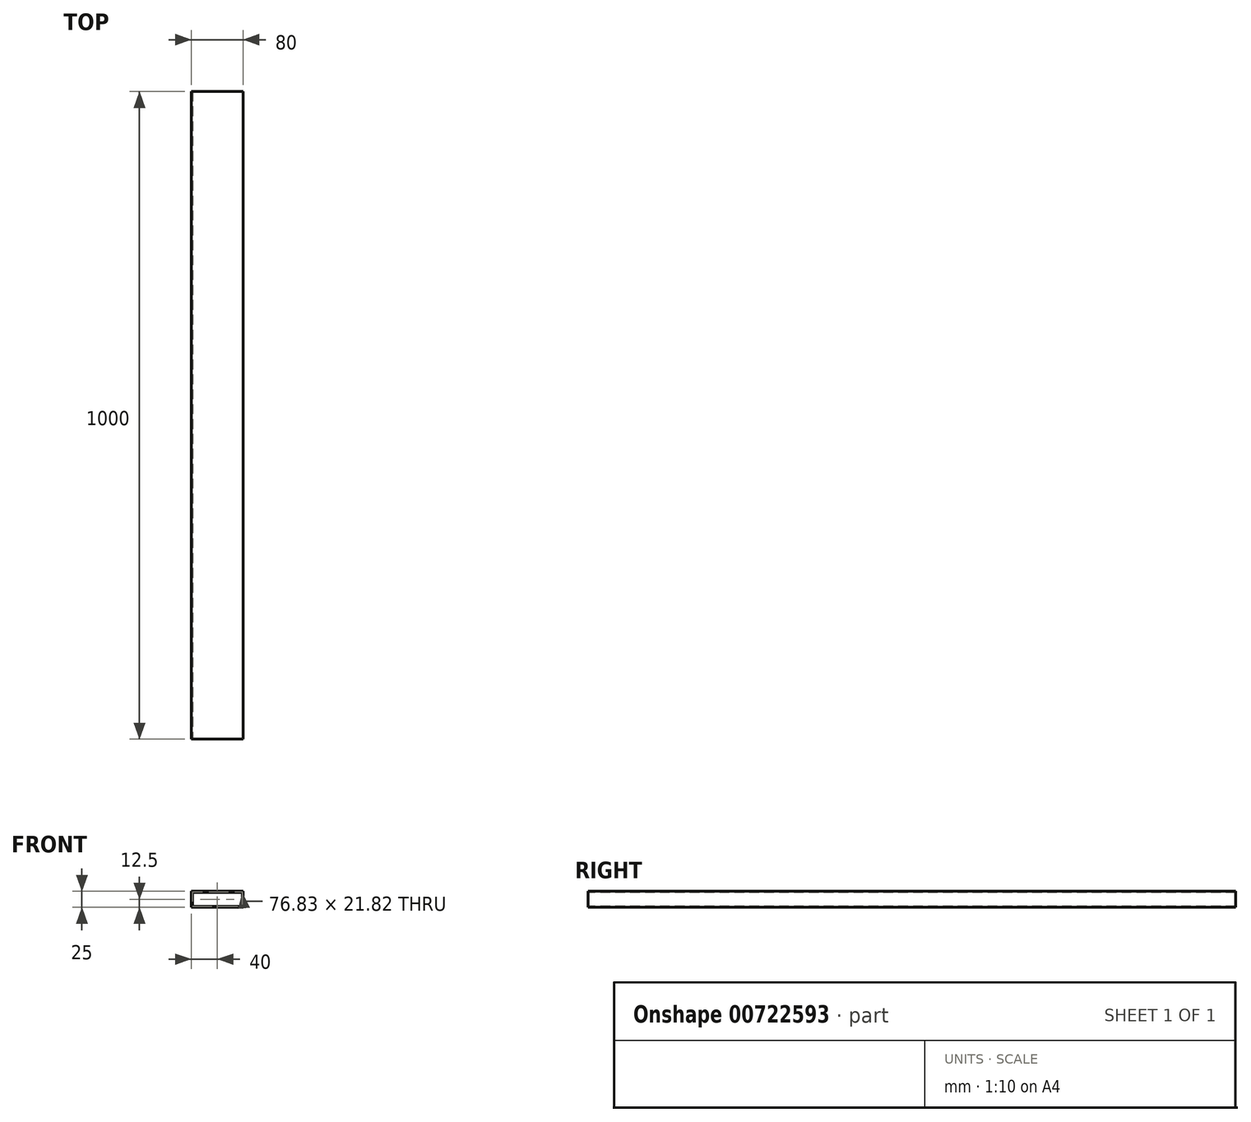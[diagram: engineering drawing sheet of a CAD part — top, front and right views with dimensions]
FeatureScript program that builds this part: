
annotation { "Feature Type Name" : "Feature", "Feature Type Description" : "" }
export const myFeature = defineFeature(function(context is Context, id is Id, definition is map)
    precondition{}
    {
        {
            var Q0;
            Q0=qCreatedBy(makeId("Front.planeOp"),FACE);
            var sketch = newSketch(context, id + "F0", { "sketchPlane" : qUnion([Q0])});
            skLineSegment(sketch, "E0.bottom", {"start": v(-40, -12.5) * mm, "end": v(40, -12.5) * mm});
            skLineSegment(sketch, "E0.top", {"start": v(-40, 12.5) * mm, "end": v(40, 12.5) * mm});
            skLineSegment(sketch, "E0.left", {"start": v(-40, -12.5) * mm, "end": v(-40, 12.5) * mm});
            skLineSegment(sketch, "E0.right", {"start": v(40, -12.5) * mm, "end": v(40, 12.5) * mm});
            skPoint(sketch, "E0.middle", {"position": v(0, 0) * mm});
            skSolve(sketch);
        }
        {
            var Q0;
            Q0 = qSketchRegion(id + "F0", true);
            extrude(context, id + "F1", {"entities" : qUnion([Q0]), "endBound" : BoundingType.SYMMETRIC, "depth" : 1000 * mm, "offsetDistance" : 25 * mm});
        }
        {
            var Q0;
            Q0=makeQuery(id+"F1.opExtrude","CAP_FACE",FACE,{"disambiguationData":[OSD([sQuery(id+"F0.wireOp",EDGE,"E0.bottom"),sQuery(id+"F0.wireOp",EDGE,"E0.top"),sQuery(id+"F0.wireOp",EDGE,"E0.left"),sQuery(id+"F0.wireOp",EDGE,"E0.right")])],"isStart":false});
            var sketch = newSketch(context, id + "F2", { "sketchPlane" : qUnion([Q0])});
            skLineSegment(sketch, "E1.bottom", {"start": v(-38.41, -10.91) * mm, "end": v(38.41, -10.91) * mm});
            skLineSegment(sketch, "E1.top", {"start": v(-38.41, 10.91) * mm, "end": v(38.41, 10.91) * mm});
            skLineSegment(sketch, "E1.left", {"start": v(-38.41, -10.91) * mm, "end": v(-38.41, 10.91) * mm});
            skLineSegment(sketch, "E1.right", {"start": v(38.41, -10.91) * mm, "end": v(38.41, 10.91) * mm});
            skPoint(sketch, "E1.middle", {"position": v(0, 0) * mm});
            skSolve(sketch);
        }
        {
            var Q0;
            Q0 = qSketchRegion(id + "F2", true);
            extrude(context, id + "F3", {"entities" : qUnion([Q0]), "operationType" : NewBodyOperationType.REMOVE, "oppositeDirection" : true, "depth" : 1000 * mm, "offsetDistance" : 25 * mm});
        }
    });
